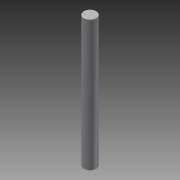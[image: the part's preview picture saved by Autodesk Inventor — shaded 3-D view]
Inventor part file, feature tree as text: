
AUTODESK INVENTOR PART (.ipt)
format: ipt  version: 2014 (Build 180170000, 170)  size: 64,512 bytes
history: native  units: in
note: dims shown in document units (in); Inventor stores cm internally (conversion verified against a paired STEP export)
features: extrude x1, sketch x1
ambient origin geometry x8: Origin, YZ Plane, XZ Plane, XY Plane, X Axis, Y Axis, Z Axis, Center Point
bodies: Solid1 (feature_tree)
feature tree (2):
  extrude  "Extrusion1"  Depth=2.0in TaperAngle=0.0deg
  sketch  "Sketch1"  dims[d0=0.19in d1=2.0in d2=0.0in]
